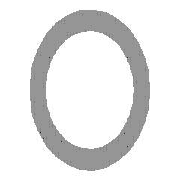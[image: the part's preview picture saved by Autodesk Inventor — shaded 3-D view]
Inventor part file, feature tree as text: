
AUTODESK INVENTOR PART (.ipt)
format: ipt  version: 2013 (Build 170138000, 138)  size: 113,664 bytes
history: native  units: mm (DEFAULTED — no unit token found)
features: other x4, plane x3, sketch x3, split x2
ambient origin geometry x8: Origin, YZ Plane, XZ Plane, XY Plane, X Axis, Y Axis, Z Axis, Center Point
bodies: Solid1 (feature_tree), Body (feature_tree)
feature tree (12):
  parser-record x1  (decoder bookkeeping rows leaked as tree rows — omitted from the tree; the rows remain in map.json)
  other  "Driven Length"
  other  "Start plane"
  other  "End plane"
  plane  "Work Plane4"
  split  "Split1"
  plane  "Work Plane5"
  split  "Split2"
  sketch  "Sketch"  dims[d2=13050.012mm d3=0.0mm d4=-0.0mm d5=13050.012mm d6=90.0deg d7=13050.012mm]
  sketch  "Sketch3"  dims[d0=33.401mm]
  plane  "Work Plane3"
  sketch  "Sketch4"  dims[d1=3.3782mm]
